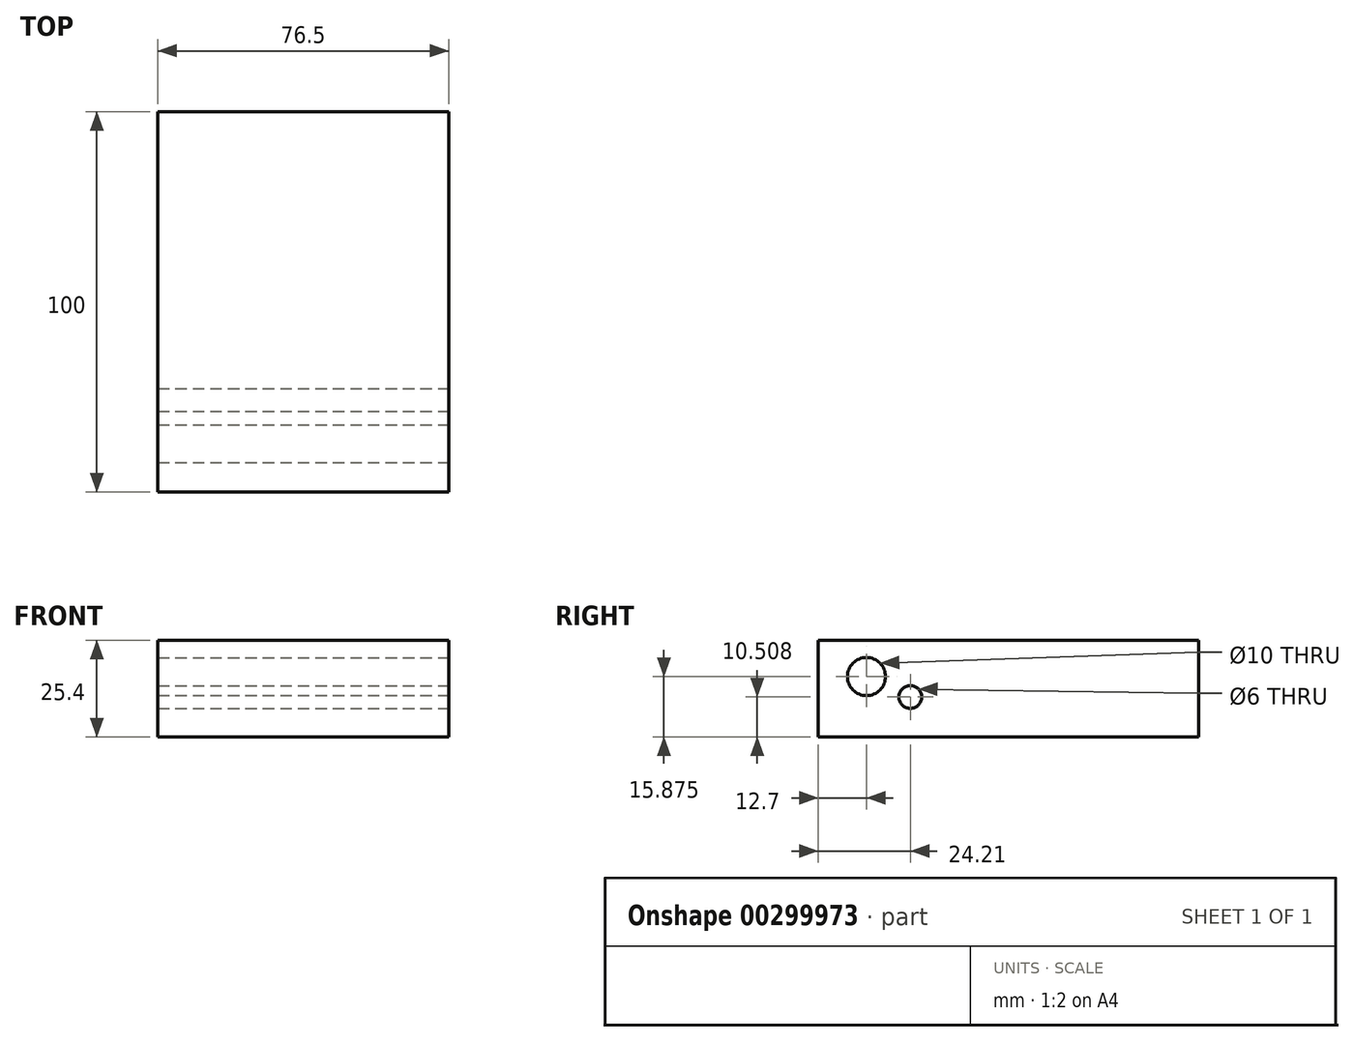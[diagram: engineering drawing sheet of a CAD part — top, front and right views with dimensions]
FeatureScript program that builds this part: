
annotation { "Feature Type Name" : "Feature", "Feature Type Description" : "" }
export const myFeature = defineFeature(function(context is Context, id is Id, definition is map)
    precondition{}
    {
        {
            var Q0;
            Q0=qCreatedBy(makeId("Top.planeOp"),FACE);
            var sketch = newSketch(context, id + "F0", { "sketchPlane" : qUnion([Q0])});
            skLineSegment(sketch, "E0.bottom", {"start": v(-38.25, 70) * mm, "end": v(38.25, 70) * mm});
            skLineSegment(sketch, "E0.top", {"start": v(-38.25, -30) * mm, "end": v(38.25, -30) * mm});
            skLineSegment(sketch, "E0.left", {"start": v(-38.25, 70) * mm, "end": v(-38.25, -30) * mm});
            skLineSegment(sketch, "E0.right", {"start": v(38.25, 70) * mm, "end": v(38.25, -30) * mm});
            skSolve(sketch);
        }
        {
            var Q0;
            Q0 = qSketchRegion(id + "F0", true);
            extrude(context, id + "F1", {"entities" : qUnion([Q0]), "depth" : 25.4 * mm, "offsetDistance" : 25 * mm});
        }
        {
            var Q0;
            Q0=makeQuery(id+"F1.opExtrude","SWEPT_FACE",FACE,{"disambiguationData":[OSD([sQuery(id+"F0.wireOp",EDGE,"E0.right")])]});
            var sketch = newSketch(context, id + "F2", { "sketchPlane" : qUnion([Q0])});
            skCircle(sketch, "E1", {"center": v(-17.3, 15.88) * mm, "radius": 5 * mm});
            skSolve(sketch);
        }
        {
            var Q0;
            Q0 = qSketchRegion(id + "F2", true);
            extrude(context, id + "F3", {"entities" : qUnion([Q0]), "operationType" : NewBodyOperationType.REMOVE, "endBound" : BoundingType.THROUGH_ALL, "oppositeDirection" : true, "depth" : 25 * mm, "offsetDistance" : 25 * mm});
        }
        {
            var Q0;
            Q0=makeQuery(id+"F1.opExtrude","SWEPT_FACE",FACE,{"disambiguationData":[OSD([sQuery(id+"F0.wireOp",EDGE,"E0.right")])]});
            var sketch = newSketch(context, id + "F4", { "sketchPlane" : qUnion([Q0])});
            skCircle(sketch, "E2", {"center": v(-5.79, 10.5) * mm, "radius": 3 * mm});
            skPoint(sketch, "E2.centerSnap0", {"position": v(8.1, 12.7) * mm});
            skCircle(sketch, "E3", {"center": v(-17.3, 15.88) * mm, "radius": 5 * mm});
            skLineSegment(sketch, "E4", {"start": v(-17.3, 15.88) * mm, "end": v(-5.79, 10.5) * mm});
            skLineSegment(sketch, "E5", {"start": v(-17.3, 15.88) * mm, "end": v(-13.47, 15.88) * mm});
            skSolve(sketch);
        }
        {
            var Q0;
            Q0=makeQuery(id+"F4.imprint","IMPRINT",FACE,{"disambiguationData":[TD([[makeQuery(id+"F4.imprint","IMPRINT",EDGE,{"derivedFrom":sQuery(id+"F4.wireOp",EDGE,"E2")}),1.0]])]});
            extrude(context, id + "F5", {"entities" : qUnion([Q0]), "operationType" : NewBodyOperationType.REMOVE, "endBound" : BoundingType.THROUGH_ALL, "oppositeDirection" : true, "depth" : 10 * mm, "offsetDistance" : 25 * mm});
        }
    });
